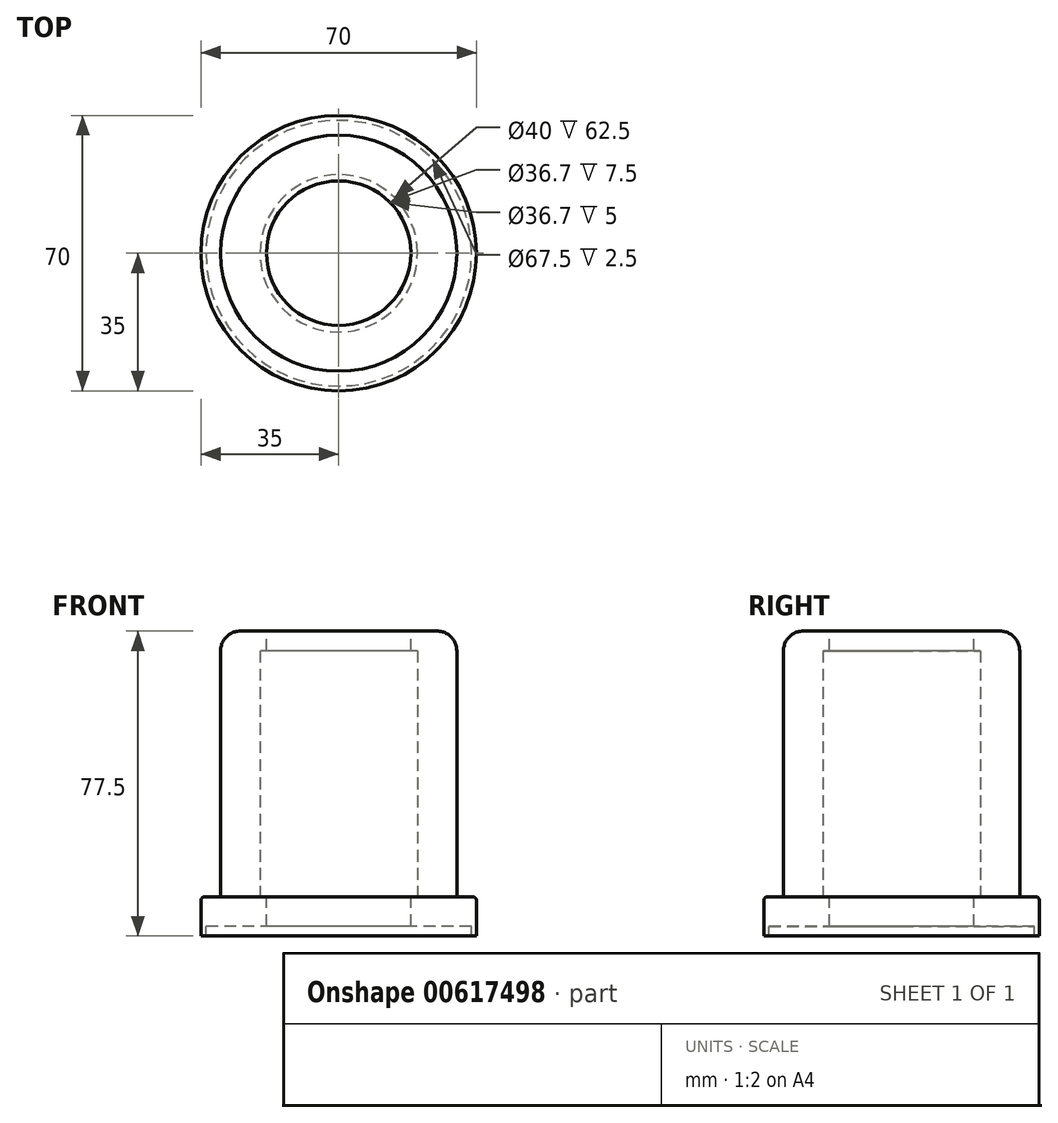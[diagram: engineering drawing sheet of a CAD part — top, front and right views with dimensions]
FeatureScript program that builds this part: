
annotation { "Feature Type Name" : "Feature", "Feature Type Description" : "" }
export const myFeature = defineFeature(function(context is Context, id is Id, definition is map)
    precondition{}
    {
        {
            var Q0;
            Q0=qCreatedBy(makeId("Top.planeOp"),FACE);
            var sketch = newSketch(context, id + "F0", { "sketchPlane" : qUnion([Q0])});
            skCircle(sketch, "E0", {"center": v(0, 0) * mm, "radius": 35 * mm});
            skSolve(sketch);
        }
        {
            var Q0;
            Q0 = qSketchRegion(id + "F0", true);
            extrude(context, id + "F1", {"entities" : qUnion([Q0]), "depth" : 7.5 * mm, "offsetDistance" : 25 * mm});
        }
        {
            var Q0;
            Q0=makeQuery(id+"F1.opExtrude","CAP_FACE",FACE,{"disambiguationData":[OSD([sQuery(id+"F0.wireOp",EDGE,"E0")])],"isStart":false});
            var sketch = newSketch(context, id + "F2", { "sketchPlane" : qUnion([Q0])});
            skCircle(sketch, "E1", {"center": v(0, 0) * mm, "radius": 18.35 * mm});
            skSolve(sketch);
        }
        {
            var Q0;
            Q0=makeQuery(id+"F2.imprint","IMPRINT",FACE,{"disambiguationData":[TD([[makeQuery(id+"F2.imprint","IMPRINT",EDGE,{"derivedFrom":sQuery(id+"F2.wireOp",EDGE,"E1")}),1.0]])]});
            extrude(context, id + "F3", {"entities" : qUnion([Q0]), "operationType" : NewBodyOperationType.REMOVE, "oppositeDirection" : true, "depth" : 25 * mm, "offsetDistance" : 25 * mm});
        }
        {
            var Q0;
            Q0=makeQuery(id+"F1.opExtrude","CAP_FACE",FACE,{"disambiguationData":[OSD([sQuery(id+"F0.wireOp",EDGE,"E0")])],"isStart":false});
            var sketch = newSketch(context, id + "F4", { "sketchPlane" : qUnion([Q0])});
            skCircle(sketch, "E2", {"center": v(0, 0) * mm, "radius": 30 * mm});
            skSolve(sketch);
        }
        {
            var Q0;
            Q0=makeQuery(id+"F4.imprint","IMPRINT",FACE,{"disambiguationData":[TD([[makeQuery(id+"F4.imprint","IMPRINT",EDGE,{"derivedFrom":sQuery(id+"F4.wireOp",EDGE,"E2")}),1.0]])]});
            var sketch = newSketch(context, id + "F5", { "sketchPlane" : qUnion([Q0])});
            skCircle(sketch, "E3", {"center": v(0, 0) * mm, "radius": 20 * mm});
            skCircle(sketch, "E4.0", {"center": v(0, 0) * mm, "radius": 30 * mm});
            skSolve(sketch);
        }
        {
            var Q0;
            Q0=makeQuery(id+"F5.imprint","IMPRINT",FACE,{"disambiguationData":[TD([[makeQuery(id+"F5.imprint","IMPRINT",EDGE,{"derivedFrom":sQuery(id+"F5.wireOp",EDGE,"E3")}),-1.0]])]});
            extrude(context, id + "F6", {"entities" : qUnion([Q0]), "operationType" : NewBodyOperationType.ADD, "depth" : 67.5 * mm, "offsetDistance" : 25 * mm});
        }
        {
            var Q0;
            Q0=makeQuery(id+"F6.opExtrude","CAP_EDGE",EDGE,{"disambiguationData":[OSD([sQuery(id+"F5.wireOp",EDGE,"E4.0")])],"isStart":false});
            fillet(context, id + "F7", {"entities" : qUnion([Q0]), "radius" : 5 * mm, "tangentPropagation" : true, "allowEdgeOverflow" : false});
        }
        {
            var Q0;
            Q0=makeQuery(id+"F6.boolean.opBoolean","SPLIT",FACE,{"disambiguationData":[TD([makeQuery(id+"F3.boolean.opBoolean","COPY",FACE,{"derivedFrom":makeQuery(id+"F3.opExtrude","SWEPT_FACE",FACE,{"disambiguationData":[OSD([sQuery(id+"F2.wireOp",EDGE,"E1")])]})})])],"derivedFrom":makeQuery(id+"F1.opExtrude","CAP_FACE",FACE,{"disambiguationData":[OSD([sQuery(id+"F0.wireOp",EDGE,"E0")])],"isStart":false})});
            extrude(context, id + "F8", {"entities" : qUnion([Q0]), "operationType" : NewBodyOperationType.ADD, "depth" : 67.5 * mm, "offsetDistance" : 25 * mm, "hasSecondDirection" : true, "secondDirectionOppositeDirection" : false, "secondDirectionDepth" : 62.5 * mm});
        }
        {
            var Q0;
            Q0=makeQuery(id+"F1.opExtrude","CAP_EDGE",EDGE,{"disambiguationData":[OSD([sQuery(id+"F0.wireOp",EDGE,"E0")])],"isStart":false});
            fillet(context, id + "F9", {"entities" : qUnion([Q0]), "radius" : 1 * mm, "tangentPropagation" : true, "allowEdgeOverflow" : false});
        }
        {
            var Q0;
            Q0=qCreatedBy(makeId("Top.planeOp"),FACE);
            cPlane(context, id + "F10", {"entities" : qUnion([Q0]), "cplaneType" : CPlaneType.OFFSET, "offset" : 75 * mm, "width" : 150 * mm, "height" : 150 * mm});
        }
        {
            var Q0;
            Q0=qCreatedBy(id+"F10.planeOp",FACE);
            var sketch = newSketch(context, id + "F11", { "sketchPlane" : qUnion([Q0])});
            skCircle(sketch, "E5.0", {"center": v(0, 0) * mm, "radius": 18.35 * mm});
            skSolve(sketch);
        }
        {
            var Q0;
            Q0=makeQuery(id+"F11.imprint","IMPRINT",FACE,{"disambiguationData":[TD([[makeQuery(id+"F11.imprint","IMPRINT",EDGE,{"derivedFrom":sQuery(id+"F11.wireOp",EDGE,"E5.0")}),1.0]])]});
            var Q1;
            Q1=sQuery(id+"F11.wireOp",EDGE,"E5.0");
            extrude(context, id + "F12", {"entities" : qUnion([Q0]), "surfaceEntities" : qUnion([Q1]), "oppositeDirection" : true, "depth" : 5 * mm, "offsetDistance" : 25 * mm});
        }
        {
            var Q0;
            Q0=makeQuery(id+"F0.imprint","IMPRINT",FACE,{"disambiguationData":[TD([[makeQuery(id+"F0.imprint","IMPRINT",EDGE,{"derivedFrom":sQuery(id+"F0.wireOp",EDGE,"E0")}),1.0]])]});
            var sketch = newSketch(context, id + "F13", { "sketchPlane" : qUnion([Q0])});
            skCircle(sketch, "E6", {"center": v(0, 0) * mm, "radius": 33.75 * mm});
            skSolve(sketch);
        }
        {
            var Q0;
            Q0=makeQuery(id+"F13.imprint","IMPRINT",FACE,{"disambiguationData":[TD([[makeQuery(id+"F13.imprint","IMPRINT",EDGE,{"derivedFrom":sQuery(id+"F13.wireOp",EDGE,"E6")}),-1.0]])]});
            extrude(context, id + "F14", {"entities" : qUnion([Q0]), "operationType" : NewBodyOperationType.ADD, "oppositeDirection" : true, "depth" : 2.5 * mm, "offsetDistance" : 25 * mm});
        }
    });
